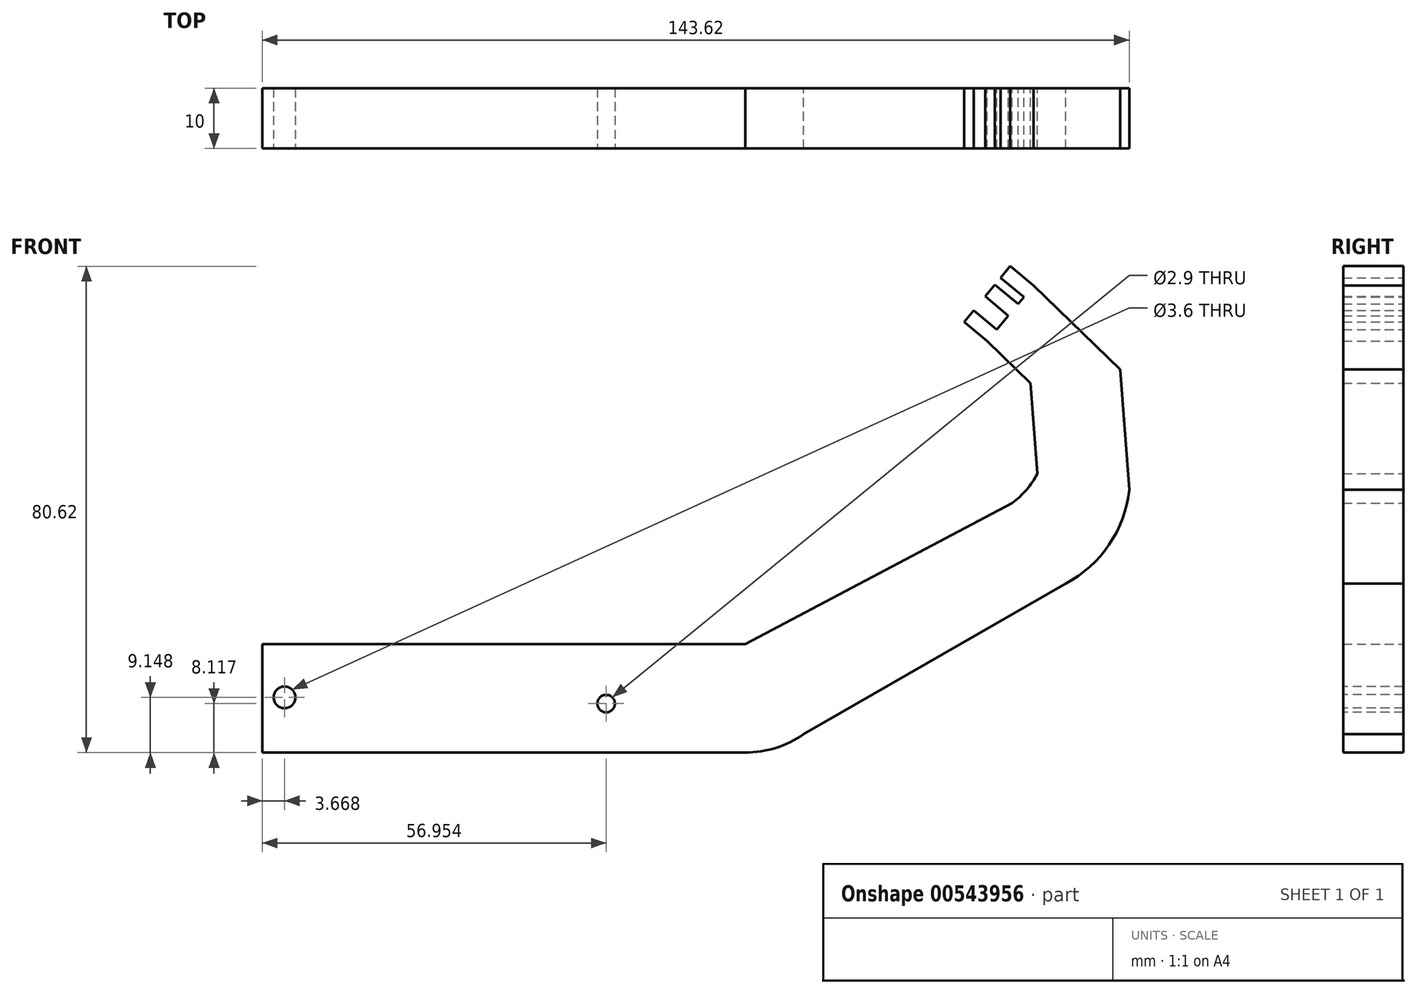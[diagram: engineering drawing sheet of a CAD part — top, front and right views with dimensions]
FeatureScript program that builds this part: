
annotation { "Feature Type Name" : "Feature", "Feature Type Description" : "" }
export const myFeature = defineFeature(function(context is Context, id is Id, definition is map)
    precondition{}
    {
        {
            var Q0;
            Q0=qCreatedBy(makeId("Front.planeOp"),FACE);
            var sketch = newSketch(context, id + "F0", { "sketchPlane" : qUnion([Q0])});
            skLineSegment(sketch, "E0.bottom", {"start": v(-20.45, -3.8) * mm, "end": v(53.55, -3.8) * mm});
            skLineSegment(sketch, "E0.top", {"start": v(-20.45, -21.8) * mm, "end": v(53.55, -21.8) * mm});
            skLineSegment(sketch, "E0.right", {"start": v(53.55, -3.8) * mm, "end": v(53.55, -21.8) * mm});
            skLineSegment(sketch, "E1", {"start": v(97.78, 19.54) * mm, "end": v(106.62, 6.2) * mm});
            skArc(sketch, "E2", {"start": v(106.62, 6.2) * mm, "mid": v(113.83, 12.66) * mm, "end": v(117.17, 21.75) * mm});
            skArc(sketch, "E3", {"start": v(97.78, 19.54) * mm, "mid": v(100.14, 21.77) * mm, "end": v(101.96, 24.47) * mm});
            skLineSegment(sketch, "E4", {"start": v(117.17, 21.75) * mm, "end": v(115.64, 41.69) * mm});
            skLineSegment(sketch, "E5", {"start": v(101.96, 24.47) * mm, "end": v(100.81, 39.42) * mm});
            skLineSegment(sketch, "E6", {"start": v(100.81, 39.42) * mm, "end": v(115.64, 41.69) * mm});
            skLineSegment(sketch, "E7", {"start": v(115.64, 41.69) * mm, "end": v(101.3, 55.63) * mm});
            skLineSegment(sketch, "E8", {"start": v(100.81, 39.42) * mm, "end": v(93.64, 46.4) * mm});
            skLineSegment(sketch, "E9", {"start": v(93.64, 46.4) * mm, "end": v(101.3, 55.63) * mm});
            skLineSegment(sketch, "E10", {"start": v(97.45, 58.82) * mm, "end": v(101.3, 55.63) * mm});
            skLineSegment(sketch, "E11", {"start": v(99.7, 53.7) * mm, "end": v(95.86, 56.9) * mm});
            skLineSegment(sketch, "E12", {"start": v(95.86, 56.9) * mm, "end": v(97.45, 58.82) * mm});
            skLineSegment(sketch, "E13", {"start": v(93.64, 46.4) * mm, "end": v(89.8, 49.59) * mm});
            skLineSegment(sketch, "E14", {"start": v(89.8, 49.59) * mm, "end": v(91.4, 51.51) * mm});
            skLineSegment(sketch, "E15", {"start": v(91.4, 51.51) * mm, "end": v(95.24, 48.32) * mm});
            skLineSegment(sketch, "E16", {"start": v(94.9, 55.74) * mm, "end": v(98.74, 52.55) * mm});
            skLineSegment(sketch, "E17", {"start": v(98.74, 52.55) * mm, "end": v(97.15, 50.62) * mm});
            skLineSegment(sketch, "E18", {"start": v(97.15, 50.62) * mm, "end": v(93.3, 53.81) * mm});
            skLineSegment(sketch, "E19", {"start": v(93.3, 53.81) * mm, "end": v(94.9, 55.74) * mm});
            skPoint(sketch, "E20.orphan", {"position": v(13.55, -3.8) * mm});
            skPoint(sketch, "E21.orphan", {"position": v(13.55, -21.8) * mm});
            skPoint(sketch, "E22.visualSharp", {"position": v(-26.45, -3.8) * mm});
            skPoint(sketch, "E23.visualSharp", {"position": v(-26.45, -21.8) * mm});
            skLineSegment(sketch, "E24", {"start": v(-20.45, -3.8) * mm, "end": v(-26.45, -3.8) * mm});
            skLineSegment(sketch, "E25", {"start": v(-20.45, -21.8) * mm, "end": v(-26.45, -21.8) * mm});
            skLineSegment(sketch, "E26", {"start": v(-26.45, -3.8) * mm, "end": v(-26.45, -21.8) * mm});
            skArc(sketch, "E27", {"start": v(53.55, -21.8) * mm, "mid": v(58.63, -21.02) * mm, "end": v(63.24, -18.77) * mm});
            skLineSegment(sketch, "E28", {"start": v(63.24, -18.77) * mm, "end": v(106.62, 6.2) * mm});
            skLineSegment(sketch, "E29", {"start": v(53.55, -3.8) * mm, "end": v(97.78, 19.54) * mm});
            skSolve(sketch);
        }
        {
            var Q0;
            Q0 = qSketchRegion(id + "F0", true);
            extrude(context, id + "F1", {"entities" : qUnion([Q0]), "endBound" : BoundingType.SYMMETRIC, "depth" : 10 * mm, "offsetDistance" : 25 * mm});
        }
        {
            var Q0;
            Q0=makeQuery(id+"F1.opExtrude","CAP_FACE",FACE,{"disambiguationData":[OSD([sQuery(id+"F0.wireOp",EDGE,"E0.bottom"),sQuery(id+"F0.wireOp",EDGE,"E0.top"),sQuery(id+"F0.wireOp",EDGE,"E0.left"),sQuery(id+"F0.wireOp",EDGE,"dFlx3WSS-NuXs-38vh-BP1l-hkDyl14ZQ1RU"),sQuery(id+"F0.wireOp",EDGE,"eLWkrCNr-kwx3-V4A0-YC1O-Lrd44Gapqwvy"),sQuery(id+"F0.wireOp",EDGE,"E2"),sQuery(id+"F0.wireOp",EDGE,"E3"),sQuery(id+"F0.wireOp",EDGE,"E4"),sQuery(id+"F0.wireOp",EDGE,"E5"),sQuery(id+"F0.wireOp",EDGE,"E7"),sQuery(id+"F0.wireOp",EDGE,"E8"),sQuery(id+"F0.wireOp",EDGE,"E9"),sQuery(id+"F0.wireOp",EDGE,"E10"),sQuery(id+"F0.wireOp",EDGE,"E11"),sQuery(id+"F0.wireOp",EDGE,"E12"),sQuery(id+"F0.wireOp",EDGE,"E13"),sQuery(id+"F0.wireOp",EDGE,"E14"),sQuery(id+"F0.wireOp",EDGE,"E15"),sQuery(id+"F0.wireOp",EDGE,"E16"),sQuery(id+"F0.wireOp",EDGE,"E18"),sQuery(id+"F0.wireOp",EDGE,"E19"),sQuery(id+"F0.wireOp",EDGE,"E22.filletArc"),sQuery(id+"F0.wireOp",EDGE,"E23.filletArc")])],"isStart":false});
            var sketch = newSketch(context, id + "F2", { "sketchPlane" : qUnion([Q0])});
            skCircle(sketch, "E30", {"center": v(30.5, -13.68) * mm, "radius": 1.45 * mm});
            skSolve(sketch);
        }
        {
            var Q0;
            Q0 = qSketchRegion(id + "F2", true);
            extrude(context, id + "F3", {"entities" : qUnion([Q0]), "operationType" : NewBodyOperationType.REMOVE, "oppositeDirection" : true, "depth" : 26 * mm, "offsetDistance" : 25 * mm});
        }
        {
            var Q0;
            Q0=makeQuery(id+"F1.opExtrude","CAP_FACE",FACE,{"disambiguationData":[OSD([sQuery(id+"F0.wireOp",EDGE,"E0.bottom"),sQuery(id+"F0.wireOp",EDGE,"E0.top"),sQuery(id+"F0.wireOp",EDGE,"E0.left"),sQuery(id+"F0.wireOp",EDGE,"dFlx3WSS-NuXs-38vh-BP1l-hkDyl14ZQ1RU"),sQuery(id+"F0.wireOp",EDGE,"eLWkrCNr-kwx3-V4A0-YC1O-Lrd44Gapqwvy"),sQuery(id+"F0.wireOp",EDGE,"E2"),sQuery(id+"F0.wireOp",EDGE,"E3"),sQuery(id+"F0.wireOp",EDGE,"E4"),sQuery(id+"F0.wireOp",EDGE,"E5"),sQuery(id+"F0.wireOp",EDGE,"E7"),sQuery(id+"F0.wireOp",EDGE,"E8"),sQuery(id+"F0.wireOp",EDGE,"E9"),sQuery(id+"F0.wireOp",EDGE,"E10"),sQuery(id+"F0.wireOp",EDGE,"E11"),sQuery(id+"F0.wireOp",EDGE,"E12"),sQuery(id+"F0.wireOp",EDGE,"E13"),sQuery(id+"F0.wireOp",EDGE,"E14"),sQuery(id+"F0.wireOp",EDGE,"E15"),sQuery(id+"F0.wireOp",EDGE,"E16"),sQuery(id+"F0.wireOp",EDGE,"E18"),sQuery(id+"F0.wireOp",EDGE,"E19"),sQuery(id+"F0.wireOp",EDGE,"E22.filletArc"),sQuery(id+"F0.wireOp",EDGE,"E23.filletArc")])],"isStart":false});
            var sketch = newSketch(context, id + "F4", { "sketchPlane" : qUnion([Q0])});
            skSolve(sketch);
        }
        {
            var Q0;
            Q0=makeQuery(id+"F4.imprint","IMPRINT",FACE,{"disambiguationData":[TD([[makeQuery(id+"F4.imprint","IMPRINT",EDGE,{"derivedFrom":makeQuery(id+"F1.opExtrude","CAP_EDGE",EDGE,{"disambiguationData":[OSD([sQuery(id+"F0.wireOp",EDGE,"E2")])],"isStart":false})}),1.0]])]});
            var sketch = newSketch(context, id + "F5", { "sketchPlane" : qUnion([Q0])});
            skCircle(sketch, "E31", {"center": v(-22.78, -12.65) * mm, "radius": 1.8 * mm});
            skSolve(sketch);
        }
        {
            var Q0;
            Q0 = qSketchRegion(id + "F5", true);
            extrude(context, id + "F6", {"entities" : qUnion([Q0]), "operationType" : NewBodyOperationType.REMOVE, "oppositeDirection" : true, "depth" : 25 * mm, "offsetDistance" : 25 * mm});
        }
    });
